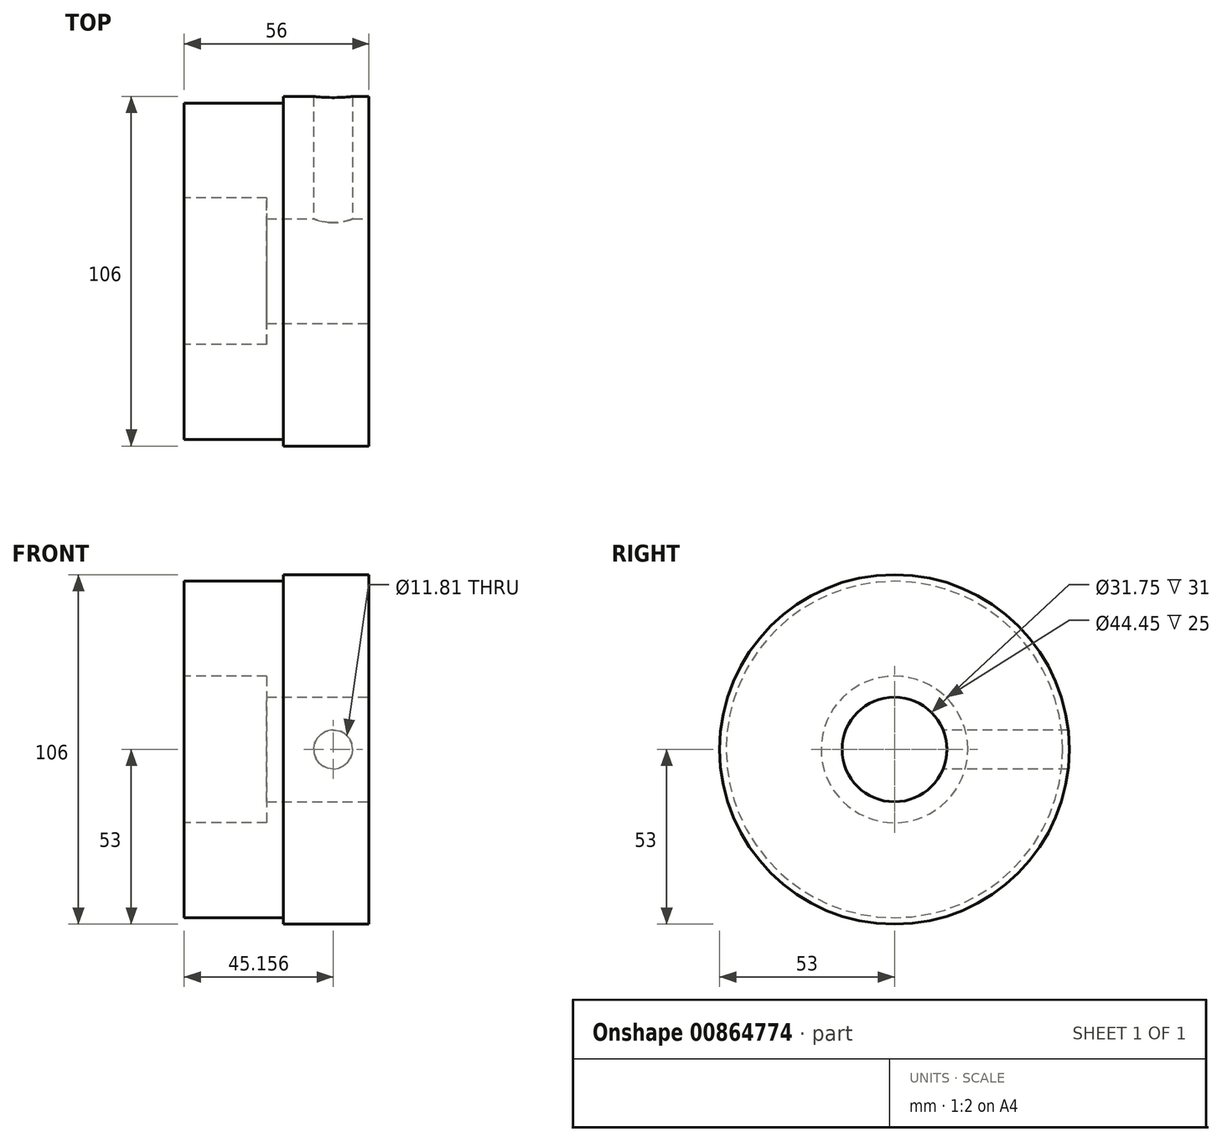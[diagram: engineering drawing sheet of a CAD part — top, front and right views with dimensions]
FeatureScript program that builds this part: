
annotation { "Feature Type Name" : "Feature", "Feature Type Description" : "" }
export const myFeature = defineFeature(function(context is Context, id is Id, definition is map)
    precondition{}
    {
        {
            var Q0;
            Q0=qCreatedBy(makeId("Right.planeOp"),FACE);
            var sketch = newSketch(context, id + "F0", { "sketchPlane" : qUnion([Q0])});
            skCircle(sketch, "E0", {"center": v(0, 0) * mm, "radius": 53 * mm});
            skSolve(sketch);
        }
        {
            var Q0;
            Q0=makeQuery(id+"F0.imprint","IMPRINT",FACE,{"disambiguationData":[TD([[makeQuery(id+"F0.imprint","IMPRINT",EDGE,{"derivedFrom":sQuery(id+"F0.wireOp",EDGE,"E0")}),1.0]])]});
            extrude(context, id + "F1", {"entities" : qUnion([Q0]), "depth" : 26 * mm, "offsetDistance" : 25 * mm});
        }
        {
            var Q0;
            Q0=makeQuery(id+"F1.opExtrude","CAP_FACE",FACE,{"disambiguationData":[OSD([sQuery(id+"F0.wireOp",EDGE,"E0")])],"isStart":true});
            var sketch = newSketch(context, id + "F2", { "sketchPlane" : qUnion([Q0])});
            skCircle(sketch, "E1", {"center": v(0, 0) * mm, "radius": 51 * mm});
            skSolve(sketch);
        }
        {
            var Q0;
            Q0 = qSketchRegion(id + "F2", true);
            extrude(context, id + "F3", {"entities" : qUnion([Q0]), "operationType" : NewBodyOperationType.ADD, "depth" : 30 * mm, "offsetDistance" : 25 * mm});
        }
        {
            var Q0;
            Q0=makeQuery(id+"F1.opExtrude","CAP_FACE",FACE,{"disambiguationData":[OSD([sQuery(id+"F0.wireOp",EDGE,"E0")])],"isStart":false});
            var sketch = newSketch(context, id + "F4", { "sketchPlane" : qUnion([Q0])});
            skCircle(sketch, "E2", {"center": v(0, 0) * mm, "radius": 15.88 * mm});
            skSolve(sketch);
        }
        {
            var Q0;
            Q0=makeQuery(id+"F4.imprint","IMPRINT",FACE,{"disambiguationData":[TD([[makeQuery(id+"F4.imprint","IMPRINT",EDGE,{"derivedFrom":sQuery(id+"F4.wireOp",EDGE,"E2")}),-1.0]])]});
            var sketch = newSketch(context, id + "F5", { "sketchPlane" : qUnion([Q0])});
            skLineSegment(sketch, "E3", {"start": v(0, 64.25) * mm, "end": v(0, -67.42) * mm, "construction": true});
            skLineSegment(sketch, "E4", {"start": v(0, 0) * mm, "end": v(48.1, -48.1) * mm, "construction": true});
            skLineSegment(sketch, "E5", {"start": v(0, 0) * mm, "end": v(-32.6, 56.46) * mm, "construction": true});
            skLineSegment(sketch, "E6", {"start": v(-62.03, 0) * mm, "end": v(69.64, 0) * mm, "construction": true});
            skLineSegment(sketch, "E7", {"start": v(0, 0) * mm, "end": v(-55.75, -32.19) * mm, "construction": true});
            skCircle(sketch, "E8", {"center": v(0, 0) * mm, "radius": 38 * mm});
            skSolve(sketch);
        }
        {
            var Q0;
            Q0=makeQuery(id+"F3.opExtrude","CAP_FACE",FACE,{"disambiguationData":[OSD([sQuery(id+"F2.wireOp",EDGE,"E1")])],"isStart":false});
            var sketch = newSketch(context, id + "F6", { "sketchPlane" : qUnion([Q0])});
            skCircle(sketch, "E9", {"center": v(0, 0) * mm, "radius": 22.23 * mm});
            skSolve(sketch);
        }
        {
            var Q0;
            Q0 = qSketchRegion(id + "F6", true);
            extrude(context, id + "F7", {"entities" : qUnion([Q0]), "operationType" : NewBodyOperationType.ADD, "depth" : 25 * mm, "offsetDistance" : 25 * mm});
        }
        {
            var Q0;
            Q0=makeQuery(id+"F4.imprint","IMPRINT",FACE,{"disambiguationData":[TD([[makeQuery(id+"F4.imprint","IMPRINT",EDGE,{"derivedFrom":sQuery(id+"F4.wireOp",EDGE,"E2")}),1.0]])]});
            extrude(context, id + "F8", {"entities" : qUnion([Q0]), "operationType" : NewBodyOperationType.REMOVE, "oppositeDirection" : true, "depth" : 31 * mm, "offsetDistance" : 25 * mm});
        }
        {
            var Q0;
            Q0=makeQuery(id+"F7.opExtrude","CAP_FACE",FACE,{"disambiguationData":[OSD([sQuery(id+"F6.wireOp",EDGE,"E9")])],"isStart":false});
            extrude(context, id + "F9", {"entities" : qUnion([Q0]), "operationType" : NewBodyOperationType.REMOVE, "oppositeDirection" : true, "depth" : 25 * mm, "offsetDistance" : 25 * mm});
        }
        {
            var Q0;
            Q0=makeQuery(id+"F9.boolean.opBoolean","MERGE",FACE,{"derivedFrom":[makeQuery(id+"F3.opExtrude","CAP_FACE",FACE,{"disambiguationData":[OSD([sQuery(id+"F2.wireOp",EDGE,"E1")])],"isStart":false}),makeQuery(id+"F9.opExtrude","CAP_FACE",FACE,{"disambiguationData":[OSD([sQuery(id+"F6.wireOp",EDGE,"E9")])],"isStart":false})]});
            var sketch = newSketch(context, id + "F10", { "sketchPlane" : qUnion([Q0])});
            skCircle(sketch, "E10", {"center": v(0, 0) * mm, "radius": 22.23 * mm});
            skSolve(sketch);
        }
        {
            var Q0;
            Q0=makeQuery(id+"F10.imprint","IMPRINT",FACE,{"disambiguationData":[TD([[makeQuery(id+"F10.imprint","IMPRINT",EDGE,{"derivedFrom":sQuery(id+"F10.wireOp",EDGE,"E10")}),1.0]])]});
            extrude(context, id + "F11", {"entities" : qUnion([Q0]), "operationType" : NewBodyOperationType.REMOVE, "oppositeDirection" : true, "depth" : 25 * mm, "offsetDistance" : 25 * mm});
        }
        {
            var Q0;
            Q0=qCreatedBy(makeId("Front.planeOp"),FACE);
            var sketch = newSketch(context, id + "F12", { "sketchPlane" : qUnion([Q0])});
            skCircle(sketch, "E11", {"center": v(15.16, 0) * mm, "radius": 5.9 * mm});
            skSolve(sketch);
        }
        {
            var Q0;
            Q0 = qSketchRegion(id + "F12", true);
            extrude(context, id + "F13", {"entities" : qUnion([Q0]), "operationType" : NewBodyOperationType.REMOVE, "oppositeDirection" : true, "depth" : 57 * mm, "offsetDistance" : 25 * mm});
        }
    });
